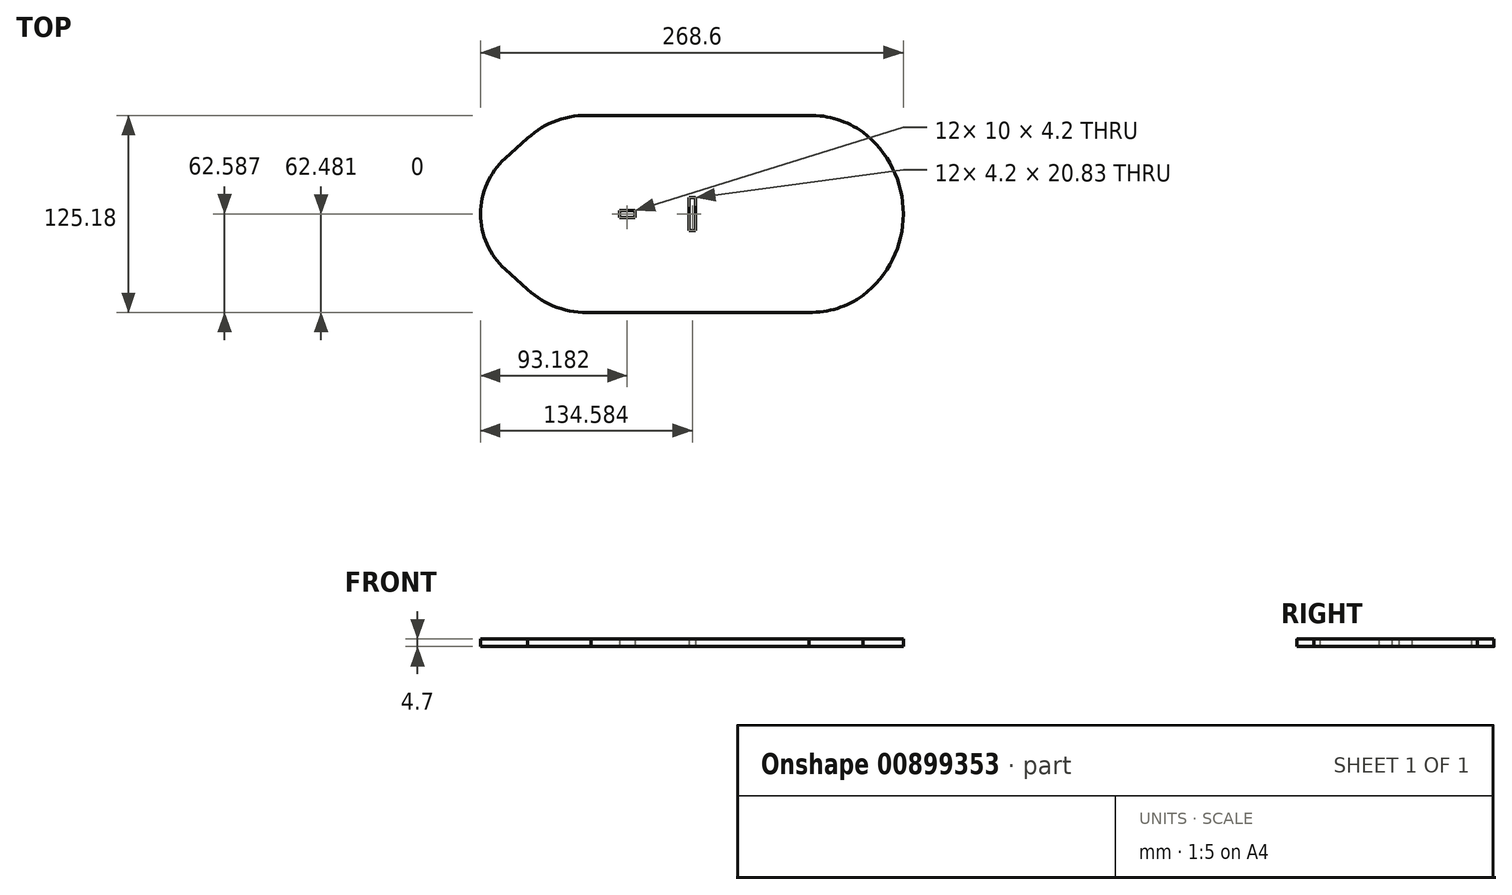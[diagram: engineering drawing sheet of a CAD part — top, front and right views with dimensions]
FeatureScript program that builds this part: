
annotation { "Feature Type Name" : "Feature", "Feature Type Description" : "" }
export const myFeature = defineFeature(function(context is Context, id is Id, definition is map)
    precondition{}
    {
        {
            var Q0;
            Q0=qCreatedBy(makeId("Top.planeOp"),FACE);
            var sketch = newSketch(context, id + "F0", { "sketchPlane" : qUnion([Q0])});
            skPoint(sketch, "E0.middle", {"position": v(-10.22, -558.41) * mm});
            skPoint(sketch, "E1.endSnap0", {"position": v(-85.22, -558.41) * mm});
            skPoint(sketch, "E2", {"position": v(-13.92, -558.41) * mm});
            skPoint(sketch, "E3.orphan", {"position": v(-104.64, -558.41) * mm});
            skPoint(sketch, "E4", {"position": v(-55.32, -558.52) * mm});
            skPoint(sketch, "E5", {"position": v(30.6, -558.41) * mm});
            skLineSegment(sketch, "E6.bottom", {"start": v(-60.32, -556.42) * mm, "end": v(-50.32, -556.42) * mm});
            skLineSegment(sketch, "E6.top", {"start": v(-60.32, -560.62) * mm, "end": v(-50.32, -560.62) * mm});
            skLineSegment(sketch, "E6.left", {"start": v(-60.32, -556.42) * mm, "end": v(-60.32, -560.62) * mm});
            skLineSegment(sketch, "E6.right", {"start": v(-50.32, -556.42) * mm, "end": v(-50.32, -560.62) * mm});
            skLineSegment(sketch, "E7.MirrorCS", {"start": v(28.29, -556.2) * mm, "end": v(28.29, -560.62) * mm});
            skLineSegment(sketch, "E8.MirrorCS", {"start": v(32.49, -556.2) * mm, "end": v(28.29, -556.2) * mm});
            skLineSegment(sketch, "E9.MirrorCS", {"start": v(32.49, -556.2) * mm, "end": v(32.49, -560.62) * mm});
            skLineSegment(sketch, "E10.MirrorCS", {"start": v(32.49, -560.62) * mm, "end": v(28.29, -560.62) * mm});
            skLineSegment(sketch, "E11.bottom", {"start": v(-16.02, -548) * mm, "end": v(-11.82, -548) * mm});
            skLineSegment(sketch, "E11.top", {"start": v(-16.02, -568.83) * mm, "end": v(-11.82, -568.83) * mm});
            skLineSegment(sketch, "E11.left", {"start": v(-16.02, -548) * mm, "end": v(-16.02, -568.83) * mm});
            skLineSegment(sketch, "E11.right", {"start": v(-11.82, -548) * mm, "end": v(-11.82, -568.83) * mm});
            skPoint(sketch, "E12.orphan", {"position": v(-85.22, -540.91) * mm});
            skPoint(sketch, "E13.orphan", {"position": v(-85.22, -575.91) * mm});
            skArc(sketch, "E14.4", {"start": v(70.5, -538.71) * mm, "mid": v(70.46, -538.69) * mm, "end": v(70.43, -538.66) * mm});
            skArc(sketch, "E15.0", {"start": v(-78.18, -495.91) * mm, "mid": v(-99.82, -499.03) * mm, "end": v(-118.52, -510.35) * mm});
            skLineSegment(sketch, "E15.1", {"start": v(-118.52, -510.35) * mm, "end": v(-132.85, -523.26) * mm});
            skLineSegment(sketch, "E15.2", {"start": v(-78.18, -495.91) * mm, "end": v(60.17, -495.91) * mm});
            skArc(sketch, "E15.3", {"start": v(-132.85, -523.26) * mm, "mid": v(-148.5, -558.41) * mm, "end": v(-132.85, -593.57) * mm});
            skLineSegment(sketch, "E15.4", {"start": v(-132.85, -593.57) * mm, "end": v(-118.52, -606.48) * mm});
            skArc(sketch, "E15.5", {"start": v(-78.18, -620.91) * mm, "mid": v(-99.82, -617.8) * mm, "end": v(-118.52, -606.48) * mm});
            skArc(sketch, "E15.6", {"start": v(94.32, -506.58) * mm, "mid": v(78.14, -498.4) * mm, "end": v(60.17, -495.91) * mm});
            skArc(sketch, "E15.7", {"start": v(94.32, -610.25) * mm, "mid": v(120.1, -558.41) * mm, "end": v(94.32, -506.58) * mm});
            skArc(sketch, "E15.8", {"start": v(94.32, -610.25) * mm, "mid": v(78.14, -618.43) * mm, "end": v(60.17, -620.91) * mm});
            skLineSegment(sketch, "E15.9", {"start": v(-78.18, -620.91) * mm, "end": v(60.17, -620.91) * mm});
            skLineSegment(sketch, "E16.trimOffspring", {"start": v(64.78, -575.46) * mm, "end": v(64.78, -575.91) * mm});
            skPoint(sketch, "E17.MirrorCS.end.orphan", {"position": v(61.06, -575.91) * mm});
            skPoint(sketch, "E18.orphan", {"position": v(67.45, -574.14) * mm});
            skPoint(sketch, "E19.orphan", {"position": v(67.45, -542.68) * mm});
            skPoint(sketch, "E20.end.orphan", {"position": v(61.06, -540.91) * mm});
            skSolve(sketch);
        }
        {
            var Q0;
            Q0 = qSketchRegion(id + "F0", true);
            var Q1;
            Q1=makeQuery(id+"F0.imprint","IMPRINT",FACE,{"disambiguationData":[TD([[makeQuery(id+"F0.imprint","IMPRINT",EDGE,{"derivedFrom":sQuery(id+"F0.wireOp",EDGE,"E6.bottom")}),1.0]])]});
            extrude(context, id + "F1", {"entities" : qUnion([Q0, Q1]), "depth" : 4.7 * mm, "offsetDistance" : 25 * mm});
        }
    });
